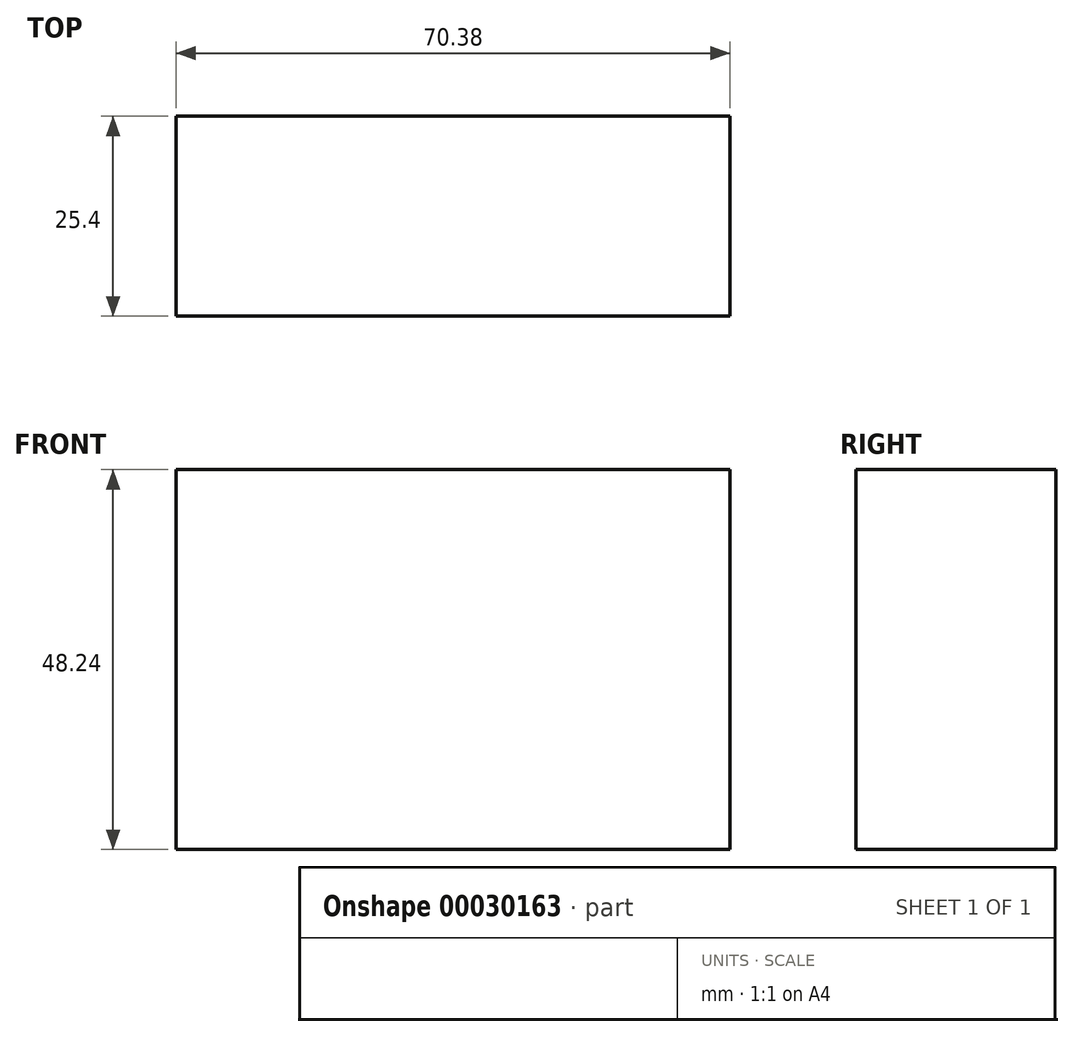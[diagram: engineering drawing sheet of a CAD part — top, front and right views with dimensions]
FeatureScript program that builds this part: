
annotation { "Feature Type Name" : "Feature", "Feature Type Description" : "" }
export const myFeature = defineFeature(function(context is Context, id is Id, definition is map)
    precondition{}
    {
        {
            var Q0;
            Q0=qCreatedBy(makeId("Front.planeOp"),FACE);
            var sketch = newSketch(context, id + "F0", { "sketchPlane" : qUnion([Q0])});
            skLineSegment(sketch, "E0.bottom", {"start": v(-27.72, 29.25) * mm, "end": v(42.66, 29.25) * mm});
            skLineSegment(sketch, "E0.top", {"start": v(-27.72, -19) * mm, "end": v(42.66, -19) * mm});
            skLineSegment(sketch, "E0.left", {"start": v(-27.72, 29.25) * mm, "end": v(-27.72, -19) * mm});
            skLineSegment(sketch, "E0.right", {"start": v(42.66, 29.25) * mm, "end": v(42.66, -19) * mm});
            skSolve(sketch);
        }
        {
            var Q0;
            Q0 = qSketchRegion(id + "F0", true);
            extrude(context, id + "F1", {"entities" : qUnion([Q0]), "depth" : 25.4 * mm});
        }
    });
